# Revit family: zzFaucet-Two_Handle-American_Standard-Colony_Pro-7075.80x_Series
name_source: partatom
category: Plumbing Fixtures
revit_build: Autodesk Revit 2014 (Build: 20130308_1515(x64)
units: mm (PartAtom-declared; Revit-internal decimal feet)

## types (2) — shared parameters
ADA Compliant = Yes
Assembly Code = D2020
CW Connection = Yes
CWFU = 1.5
Cold Water Connection Diameter = 3/8"
Cold Water Connection Radius = 3/16"
Cold Water Connection Width = 4"
Default Elevation = 0"
Flow Rate = 1.2 gpm (4.5 L/min.)
HW Connection = Yes
HWFU = 1.5
Height = 3 7/8"
Hot Water Connection Diameter = 0"
Hot Water Connection Radius = 3/16"
Hot Water Connection Width = 4"
Installation Type = Deck Mounted
Length = 6 1/2"
Manufacturer = American Standard
Material = Metal-American Standard-002-Polished Chrome
Plug Button Visibility = No
Price = Prices may vary. Please consult Manufacturer Representative for most up-to-date price list.
Product Page URL = https://www.americanstandard-us.com
URL = https://www.americanstandard-us.com
Vent Connection = No
WFU = 2
Warranty Information = Limited Lifetime Warranty
Waste Connection = No
Width = 14 1/8"

## per-type parameters (varying)
| type | Description |
| 7075.800 | Colony® PRO Two-Handle Widespread Lavatory Faucet with metal pop-up drain. |
| 7075.802 | Colony® PRO Two-Handle Widespread Lavatory Faucet with 50/50 pop-up drain. |

note: column(s) folded — value = type name in every type: Model

## geometry (parser evidence)
native form markers: Sweep x1
no freeform markers — native parametric forms only
